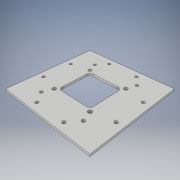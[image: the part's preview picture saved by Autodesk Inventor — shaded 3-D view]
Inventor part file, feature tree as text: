
AUTODESK INVENTOR PART (.ipt)
format: ipt  version: 2018 (Build 220112000, 112)  size: 144,384 bytes
history: native  units: mm
features: extrude x1, sketch x1
ambient origin geometry x8: Origin, YZ Plane, XZ Plane, XY Plane, X Axis, Y Axis, Z Axis, Center Point
bodies: Body1 (feature_tree)
feature tree (2):
  extrude  "Vysunutí2"  Depth=120.0mm
  sketch  "Náčrt2"
